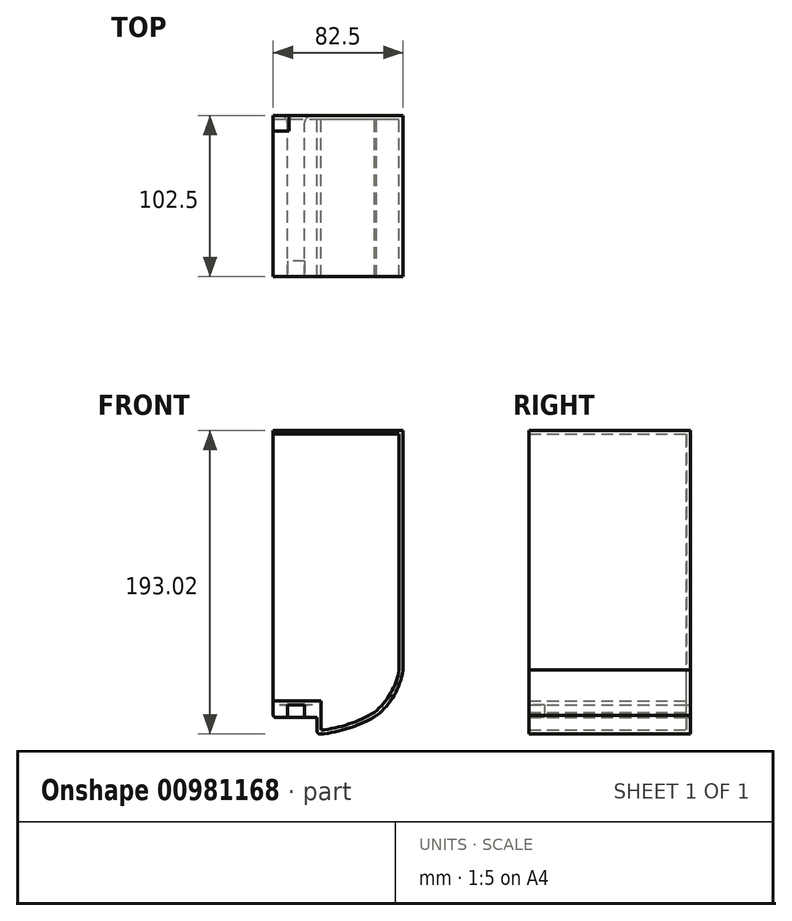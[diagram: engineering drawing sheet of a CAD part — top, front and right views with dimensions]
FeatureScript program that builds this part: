
annotation { "Feature Type Name" : "Feature", "Feature Type Description" : "" }
export const myFeature = defineFeature(function(context is Context, id is Id, definition is map)
    precondition{}
    {
        {
            var Q0;
            Q0=qCreatedBy(makeId("Front.planeOp"),FACE);
            var sketch = newSketch(context, id + "F0", { "sketchPlane" : qUnion([Q0])});
            skLineSegment(sketch, "E0", {"start": v(-82.5, 0) * mm, "end": v(-73.5, 0) * mm});
            skLineSegment(sketch, "E1", {"start": v(-73.5, 0) * mm, "end": v(-73.5, 8) * mm});
            skLineSegment(sketch, "E2", {"start": v(-73.5, 8) * mm, "end": v(-62.5, 8) * mm});
            skLineSegment(sketch, "E3", {"start": v(-62.5, 8) * mm, "end": v(-62.5, 0) * mm});
            skPoint(sketch, "E4", {"position": v(-82.5, 0) * mm});
            skPoint(sketch, "E5", {"position": v(-82.5, 53.54) * mm});
            skLineSegment(sketch, "E6", {"start": v(-82.5, 0) * mm, "end": v(-82.5, 182.5) * mm});
            skLineSegment(sketch, "E7", {"start": v(-82.5, 182.5) * mm, "end": v(0, 182.5) * mm});
            skArc(sketch, "E8.0", {"start": v(-2.36, -23.25) * mm, "mid": v(-2.11, -23.23) * mm, "end": v(-1.86, -23.2) * mm});
            skLineSegment(sketch, "E9.0", {"start": v(-30.32, -7.59) * mm, "end": v(-29.66, -7.4) * mm});
            skPoint(sketch, "E10.orphan", {"position": v(6.66, 0) * mm});
            skLineSegment(sketch, "E11", {"start": v(0, 182.5) * mm, "end": v(0, 30.16) * mm});
            skArc(sketch, "E12", {"start": v(-16.73, 1.32) * mm, "mid": v(-5.61, 14.15) * mm, "end": v(0, 30.16) * mm});
            skPoint(sketch, "E13.orphan", {"position": v(-29.9, -9.81) * mm});
            skLineSegment(sketch, "E14", {"start": v(-62.5, 0) * mm, "end": v(-54.6, 0) * mm});
            skLineSegment(sketch, "E15", {"start": v(-54.6, 0) * mm, "end": v(-54.6, -10.7) * mm});
            skPoint(sketch, "E16.orphan", {"position": v(0, 22.02) * mm});
            skArc(sketch, "E17", {"start": v(-54.6, -10.7) * mm, "mid": v(-34.96, -6.93) * mm, "end": v(-16.73, 1.32) * mm});
            skPoint(sketch, "E18.end.orphan", {"position": v(-52.1, -9.81) * mm});
            skLineSegment(sketch, "E19.trimOffspring", {"start": v(-52.1, -9.81) * mm, "end": v(-52.1, -10.7) * mm});
            skPoint(sketch, "E20.orphan", {"position": v(-54.6, -8.2) * mm});
            skSolve(sketch);
        }
        {
            var Q0;
            Q0=makeQuery(id+"F0.imprint","IMPRINT",FACE,{"disambiguationData":[TD([[makeQuery(id+"F0.imprint","IMPRINT",EDGE,{"derivedFrom":sQuery(id+"F0.wireOp",EDGE,"E0")}),1.0]])]});
            extrude(context, id + "F1", {"entities" : qUnion([Q0]), "offsetDistance" : 25 * mm, "depth" : 2.5 * mm});
        }
        {
            var Q0;
            Q0 = qSketchRegion(id + "F0", true);
            extrude(context, id + "F2", {"entities" : qUnion([Q0]), "operationType" : NewBodyOperationType.ADD, "depth" : 2.2 * mm, "offsetDistance" : 25 * mm});
        }
        {
            var Q0;
            Q0=makeQuery(id+"F1.opExtrude","CAP_FACE",FACE,{"disambiguationData":[OSD([sQuery(id+"F0.wireOp",EDGE,"E0"),sQuery(id+"F0.wireOp",EDGE,"E1"),sQuery(id+"F0.wireOp",EDGE,"E2"),sQuery(id+"F0.wireOp",EDGE,"E3"),sQuery(id+"F0.wireOp",EDGE,"E6"),sQuery(id+"F0.wireOp",EDGE,"E7"),sQuery(id+"F0.wireOp",EDGE,"E11"),sQuery(id+"F0.wireOp",EDGE,"E12"),sQuery(id+"F0.wireOp",EDGE,"E14"),sQuery(id+"F0.wireOp",EDGE,"E15"),sQuery(id+"F0.wireOp",EDGE,"E17")])],"isStart":false});
            var sketch = newSketch(context, id + "F3", { "sketchPlane" : qUnion([Q0])});
            skLineSegment(sketch, "E21.0", {"start": v(-52.1, 0) * mm, "end": v(-52.1, -7.97) * mm});
            skLineSegment(sketch, "E21.1", {"start": v(-82.5, 180) * mm, "end": v(-2.5, 180) * mm});
            skLineSegment(sketch, "E21.2", {"start": v(-2.5, 180) * mm, "end": v(-2.5, 30.35) * mm});
            skArc(sketch, "E21.3", {"start": v(-18.16, 3.38) * mm, "mid": v(-7.78, 15.39) * mm, "end": v(-2.5, 30.35) * mm});
            skArc(sketch, "E21.4", {"start": v(-52.1, -7.97) * mm, "mid": v(-34.5, -4.15) * mm, "end": v(-18.16, 3.38) * mm});
            skLineSegment(sketch, "E22", {"start": v(-52.1, 0) * mm, "end": v(-52.1, 8) * mm});
            skLineSegment(sketch, "E23", {"start": v(-62.5, 0) * mm, "end": v(-62.5, 8) * mm});
            skLineSegment(sketch, "E24", {"start": v(-62.5, 10.5) * mm, "end": v(-82.5, 10.5) * mm});
            skLineSegment(sketch, "E25", {"start": v(-62.5, 10.5) * mm, "end": v(-52.1, 10.5) * mm});
            skLineSegment(sketch, "E26", {"start": v(-52.1, 0) * mm, "end": v(-52.1, 10.5) * mm});
            skLineSegment(sketch, "E27", {"start": v(-82.5, 10.5) * mm, "end": v(-82.5, 0) * mm});
            skLineSegment(sketch, "E28", {"start": v(-82.5, 0) * mm, "end": v(-73.5, 0) * mm});
            skLineSegment(sketch, "E29", {"start": v(-73.5, 0) * mm, "end": v(-73.5, 8) * mm});
            skLineSegment(sketch, "E30", {"start": v(-73.5, 8) * mm, "end": v(-62.5, 8) * mm});
            skLineSegment(sketch, "E31", {"start": v(-62.5, 0) * mm, "end": v(-54.6, 0) * mm});
            skLineSegment(sketch, "E32", {"start": v(-54.6, 0) * mm, "end": v(-54.6, -10.7) * mm});
            skSolve(sketch);
        }
        {
            var Q0;
            Q0 = qSketchRegion(id + "F3", true);
            var Q1;
            {var subQ3=sQuery(id+"F3.wireOp",EDGE,"E21.0");Q1=makeQuery(id+"F3.imprint","IMPRINT",FACE,{"disambiguationData":[TD([[makeQuery(id+"F3.imprint","IMPRINT",EDGE,{"derivedFrom":subQ3}),-1.0]])]});}
            extrude(context, id + "F4", {"entities" : qUnion([Q0, Q1]), "operationType" : NewBodyOperationType.ADD, "depth" : 100 * mm, "offsetDistance" : 25 * mm});
        }
        {
            var Q0;
            Q0=makeQuery(id+"F4.opExtrude","CAP_FACE",FACE,{"disambiguationData":[OSD([sQuery(id+"F0.wireOp",EDGE,"E6"),sQuery(id+"F0.wireOp",EDGE,"E7"),sQuery(id+"F0.wireOp",EDGE,"E11"),sQuery(id+"F0.wireOp",EDGE,"E12"),sQuery(id+"F0.wireOp",EDGE,"E17"),sQuery(id+"F3.wireOp",EDGE,"E21.0"),sQuery(id+"F3.wireOp",EDGE,"E21.1"),sQuery(id+"F3.wireOp",EDGE,"E21.2"),sQuery(id+"F3.wireOp",EDGE,"E21.3"),sQuery(id+"F3.wireOp",EDGE,"E21.4"),sQuery(id+"F3.wireOp",EDGE,"E23"),sQuery(id+"F3.wireOp",EDGE,"E24"),sQuery(id+"F3.wireOp",EDGE,"E25"),sQuery(id+"F3.wireOp",EDGE,"E26"),sQuery(id+"F3.wireOp",EDGE,"E27"),sQuery(id+"F3.wireOp",EDGE,"E28"),sQuery(id+"F3.wireOp",EDGE,"E29"),sQuery(id+"F3.wireOp",EDGE,"E30"),sQuery(id+"F3.wireOp",EDGE,"E31"),sQuery(id+"F3.wireOp",EDGE,"E32")])],"isStart":false});
            var sketch = newSketch(context, id + "F5", { "sketchPlane" : qUnion([Q0])});
            skLineSegment(sketch, "E33", {"start": v(-73.5, 8) * mm, "end": v(-62.5, 8) * mm});
            skLineSegment(sketch, "E34", {"start": v(-62.5, 8) * mm, "end": v(-62.5, 0) * mm});
            skLineSegment(sketch, "E35", {"start": v(-62.5, 0) * mm, "end": v(-73.5, 0) * mm});
            skLineSegment(sketch, "E36", {"start": v(-73.5, 0) * mm, "end": v(-73.5, 8) * mm});
            skSolve(sketch);
        }
        {
            var Q0;
            Q0=makeQuery(id+"F5.imprint","IMPRINT",FACE,{"disambiguationData":[TD([[makeQuery(id+"F5.imprint","IMPRINT",EDGE,{"derivedFrom":sQuery(id+"F5.wireOp",EDGE,"E33")}),-1.0]])]});
            extrude(context, id + "F6", {"entities" : qUnion([Q0]), "oppositeDirection" : true, "depth" : 10 * mm, "offsetDistance" : 25 * mm});
        }
        {
            var Q0;
            Q0=makeQuery(id+"F1.opExtrude","CAP_EDGE",EDGE,{"disambiguationData":[OSD([sQuery(id+"F0.wireOp",EDGE,"E3")])],"isStart":true});
            var Q1;
            Q1=makeQuery(id+"F1.opExtrude","CAP_EDGE",EDGE,{"disambiguationData":[OSD([sQuery(id+"F0.wireOp",EDGE,"E1")])],"isStart":true});
            fillet(context, id + "F7", {"entities" : qUnion([Q0, Q1]), "radius" : 5 * mm, "tangentPropagation" : true, "allowEdgeOverflow" : false});
        }
        {
            var Q0;
            {var subQ0=sQuery(id+"F0.wireOp",EDGE,"E17");Q0=makeQuery(id+"F4.boolean.opBoolean","MERGE",EDGE,{"derivedFrom":[makeQuery(id+"F1.opExtrude","SWEPT_EDGE",EDGE,{"disambiguationData":[OSD([sQuery(id+"F0.wireOp",EDGE,"E15"),subQ0])]}),makeQuery(id+"F4.opExtrude","SWEPT_EDGE",EDGE,{"disambiguationData":[OSD([subQ0,sQuery(id+"F3.wireOp",EDGE,"E32")])]})]});}
            var Q1;
            Q1=makeQuery(id+"F4.boolean.opBoolean","MERGE",EDGE,{"derivedFrom":[makeQuery(id+"F1.opExtrude","SWEPT_EDGE",EDGE,{"disambiguationData":[OSD([sQuery(id+"F0.wireOp",EDGE,"E0"),sQuery(id+"F0.wireOp",EDGE,"E6")])]}),makeQuery(id+"F4.opExtrude","SWEPT_EDGE",EDGE,{"disambiguationData":[OSD([sQuery(id+"F3.wireOp",EDGE,"E27"),sQuery(id+"F3.wireOp",EDGE,"E28")])]})]});
            fillet(context, id + "F8", {"entities" : qUnion([Q0, Q1]), "radius" : 2 * mm, "tangentPropagation" : true, "allowEdgeOverflow" : false});
        }
        {
            var Q0;
            {var subQ0=sQuery(id+"F0.wireOp",EDGE,"E7");Q0=makeQuery(id+"F4.boolean.opBoolean","MERGE",FACE,{"derivedFrom":[makeQuery(id+"F1.opExtrude","SWEPT_FACE",FACE,{"disambiguationData":[OSD([subQ0])]}),makeQuery(id+"F4.opExtrude","SWEPT_FACE",FACE,{"disambiguationData":[OSD([subQ0])]})]});}
            var sketch = newSketch(context, id + "F9", { "sketchPlane" : qUnion([Q0])});
            skLineSegment(sketch, "E37.bottom", {"start": v(-82.5, 0) * mm, "end": v(-72.5, 0) * mm});
            skLineSegment(sketch, "E37.top", {"start": v(-82.5, -10) * mm, "end": v(-72.5, -10) * mm});
            skLineSegment(sketch, "E37.left", {"start": v(-82.5, 0) * mm, "end": v(-82.5, -10) * mm});
            skLineSegment(sketch, "E37.right", {"start": v(-72.5, 0) * mm, "end": v(-72.5, -10) * mm});
            skCircle(sketch, "E38", {"center": v(-77.5, -5) * mm, "radius": 2.5 * mm});
            skSolve(sketch);
        }
        {
            var Q0;
            Q0 = qSketchRegion(id + "F9", true);
            var Q1;
            Q1=makeQuery(id+"F9.imprint","IMPRINT",FACE,{"disambiguationData":[TD([[makeQuery(id+"F9.imprint","IMPRINT",EDGE,{"derivedFrom":sQuery(id+"F9.wireOp",EDGE,"E38")}),1.0]])]});
            extrude(context, id + "F10", {"entities" : qUnion([Q0, Q1]), "operationType" : NewBodyOperationType.REMOVE, "oppositeDirection" : true, "depth" : 0.4 * mm, "offsetDistance" : 25 * mm});
        }
    });
